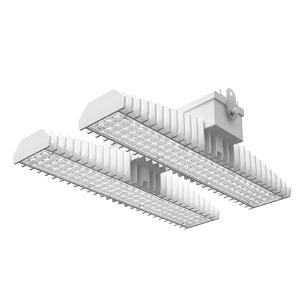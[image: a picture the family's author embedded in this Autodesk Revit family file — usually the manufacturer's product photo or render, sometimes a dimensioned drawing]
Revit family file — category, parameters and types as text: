
# Revit family: 3f_filippi_-_3f_lem_ampio_3f_filippi_-_59158_a0811_-_3f_lem_2_led_100-865_cr_ampio___vt_7fc4
name_source: partatom
category: Lighting Fixtures
units: mm (PartAtom-declared; Revit-internal decimal feet)

## family parameters
Cut with Voids When Loaded = No
Host = Face
Light Source = No
Part Type = Normal
Room Calculation Point = No
Round Connector Dimension = Use Diameter
Shared = No

## types (1)
- 3F Filippi - 3F LEM Ampio (1 x LED, 15821 lm, 109 W, 6500 K)
    Apparent Load = 109 VA
    Approval mark = CE
    CIE Flux Codes = 60 92 99 100 100
    Color Rendering = 80
    Color Temperature = 6500 K
    Control Gear = Electronic ballast
    Default Elevation = 1800 mm
    Description = Industrial luminaire with high light output and high luminous efficiency designed with the most innovative technologies for environments with temperature up to 55°C.

ILLUMINOTECHNICAL
Luminous efficiency 100% (DLOR 99%, ULOR 1%).
Initial luminous flux of the luminaire 15821 lm.
Direct symmetric wide distribution: the illuminated area has a rectangular shape.
Installation Interdistance Transv.D = 1.58 x hu - Long.D = 1.45 x hu.
Tabular UGR (CIE 117 - 4H-8H; S=0.25H; 70/50/20): RUG 22.2 - 23.2.
Beam angle: 93° - 99°.
Luminous efficacy 145 lm/W.
Lifetime (L93/B10): 30000 h. (tq+25°C)
Lifetime (L90/B10): 50000 h. (tq+25°C)
Lifetime (L85/B10): 80000 h. (tq+25°C)
Lifetime (L80/B10): 100000 h. (tq+25°C)
Lifetime (L85/B10): 50000 h. (tq+55°C)
Sudden decreased luminous flux after 50000 hours: 0% (C0).
Photobiological safety in compliance with IEC/TR 62778: RG0 risk exempt, (IEC 62471).
In compliance with IEC/EN 62722-2-1 - IEC/EN 62717 standards.

SOURCE
2 Mid-Power linear LED modules 50W/865.
Energy efficiency class (UE 2019/2020 - UE 2019/2015): C.
CIE 13.3 Colour rendering index: CRI >80 (R9 <50%).
IES TM-30 Fidelity Index: Rf = 84 Rg = 95.
CCT nominal colour temperature 6500 K.
Colour initial tolerance (MacAdam): SDCM 3.

MECHANICAL
Passive modular heatsinks in die-casted aluminium, painted in white colour.
To optimize the thermal management of the LED module, the heatsinks are oversized and provided with self-cleaning of cooling fins.
Wiring body in aluminium and galvanised steel anchored solidly to the sinks and thermally separated.
3F Lens lenses with high luminous efficiency, transparent methacrylate (PMMA), fixed to the LED modules.
Fixing brackets in stainless steel.
Luminaire with limited surface temperature. - D - (EN 60598-2-24)
Dimensions: 470x542 mm, height 133 mm. Weight 10.144 kg.
IP65 protection degree.
Mechanical strength to impacts IK06 (1 joule).
Glow-wire test resistance 650°C.

ELECTRICAL
Halogen Free electronic wiring 230V-50/60Hz, power factor 0.97, THD <25%, constant output current, class I, 1 driver.
Power of the luminaire 109 W.
ENEC - CE.
SAFE FLICKER: PstLM=<1 and SVM=<0.4 (IEC TR 61547-1 and IEC TR 63158), to ensure a more comfortable and safe light.
Luminaire compliant with EN 60598-2-22 for power supply from a centralised emergency system CPSS (Central Power Supply System), not incorporated in the luminaire - high risk areas excluded. The default power and flux are 100% in AC and 100% in DC.
Ambient temperature from -30°C to +55°C.
Temperature class T6 max 85°C.
Quick connection via M20 3P connector with 9-13 mm tightening range.
Power unit positioned on a separate compartment by the LED module to ensure optimum temperatures of cabling components, to be inspectable and maintainable.
Relative humidity UR: <85%.

INSTALLATION
Ceiling / Suspended / Wall.
All accessories dedicated to this product are available on the Catalog and on our website www.3F-Filippi.com.

ACCESSORIES
A0811 - VT transparent glass, tempered, not flammable, with sealing gasket.
One required for each light module. The pack contains 10 pieces.

APPLICATIONS
In commercial environments, exhibition and industrial areas, stores, open areas.
Applications with high ambient temperature up to 55°C.
Environments in which it is necessary a total protection against falling fragments (eg environments with foodstuffs or machines with moving parts or with extreme temperature changes), use luminaires with polycarbonate lenses.

WARNING
Fixture not suitable for cold stores with an ambient temperature <0°C and/or relative humidity >85%.
Luminaire designed for disposal/recycling at end-of-life.
Replaceable (LED only) light source by a professional. Replaceable control gear by a professional.
    Height = 133 mm  [stored 0.436352 ft]
    Lamp = 1 x LED
    Lamp Light Flux = 15821 lm
    Lamp Power = 109 W
    Lamp count = 1
    Length = 470 mm
    Lifetime = 50000 h
    Luminous efficacy = 145 lm/W
    Manufacturer = 3F Filippi
    ModVariant = No
    Model = 3F Filippi - 59158+A0811 - 3F LEM 2 LED 100-865 CR AMPIO + VT
    Mounting Place = Ceiling
    Mounting Type = Pendant
    Number of Poles = 1
    OnlyDefault = Yes
    Power Factor = 1
    Product Name = 3F Filippi - 3F LEM Ampio
    Product group = pendant luminaire
    ProductGroupID = 9
    Protection Class = Protection class I
    Protection Degree = IP 65
    RLX_Detail_Level = 1
    RLX_Emergency_Light_Flux = 0 lm
    RLX_Emergency_Type = 0
    RLX_Emergency_Type_DB = No
    RlxData = <blob elided: 102733 chars, md5=162d7048>
    Socket = socket
    Standby Power = 0 W
    System Light Flux = 15821 lm
    System Power = 109 W
    Type Comments = Product without accessories
    Type Image = 3f_filippi_-_lem_2__a0811.jpg
    URL = http://relux.com
    VarID = ---
    Voltage = 0 V
    Weight = 0.00 kg
    Width = 542 mm

note: [stored X ft] marks values corroborated as IEEE doubles in the binary element streams (Revit-internal decimal feet)

## geometry (parser evidence)
native form markers: Blend x4, Sweep x11
no freeform markers — native parametric forms only
